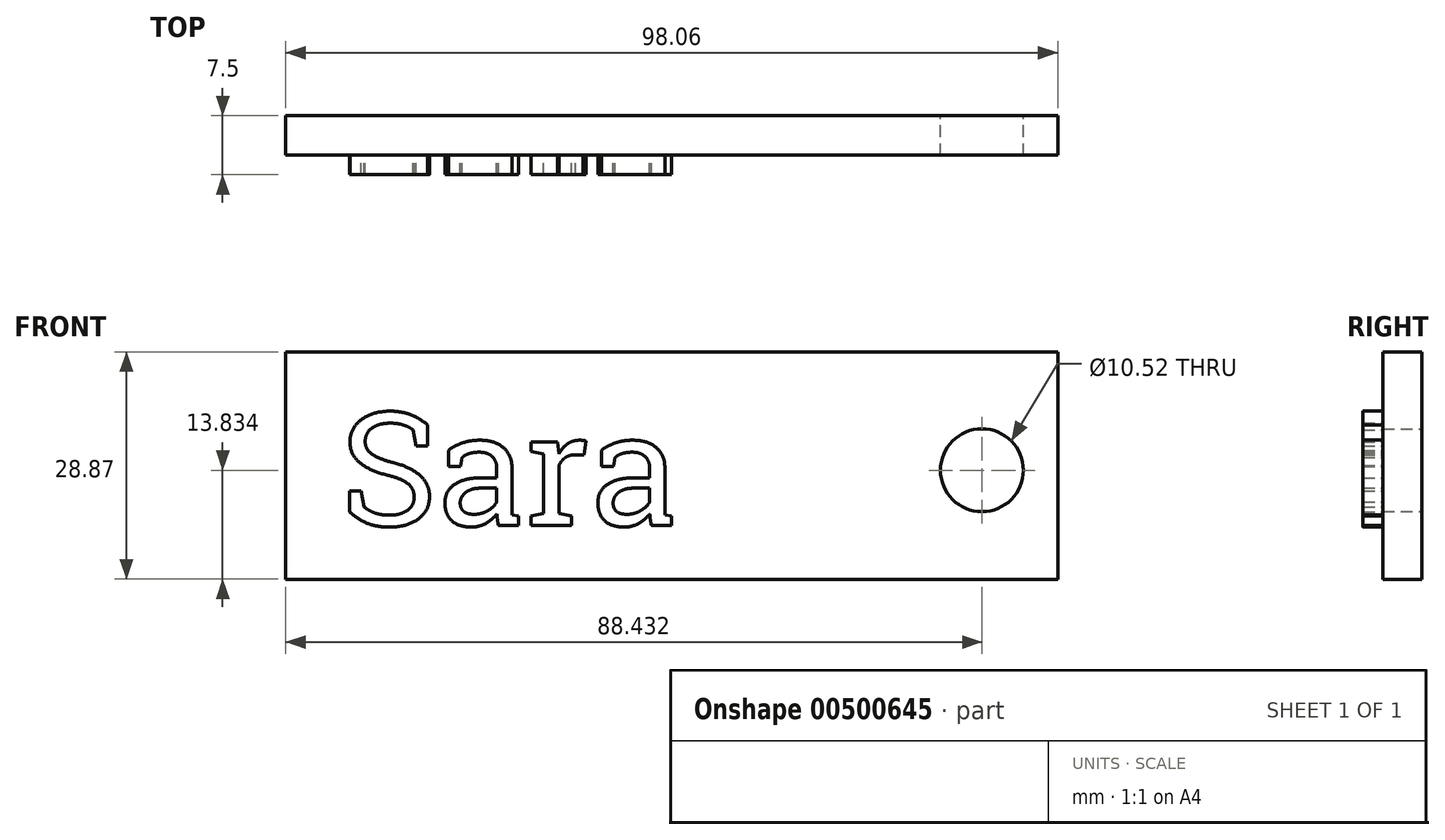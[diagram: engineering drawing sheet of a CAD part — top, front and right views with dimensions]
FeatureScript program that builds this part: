
annotation { "Feature Type Name" : "Feature", "Feature Type Description" : "" }
export const myFeature = defineFeature(function(context is Context, id is Id, definition is map)
    precondition{}
    {
        {
            var Q0;
            Q0=qCreatedBy(makeId("Front.planeOp"),FACE);
            var sketch = newSketch(context, id + "F0", { "sketchPlane" : qUnion([Q0])});
            skLineSegment(sketch, "E0.bottom", {"start": v(-64.67, 46.92) * mm, "end": v(33.39, 46.92) * mm});
            skLineSegment(sketch, "E0.top", {"start": v(-64.67, 18.05) * mm, "end": v(33.39, 18.05) * mm});
            skLineSegment(sketch, "E0.left", {"start": v(-64.67, 46.92) * mm, "end": v(-64.67, 18.05) * mm});
            skLineSegment(sketch, "E0.right", {"start": v(33.39, 46.92) * mm, "end": v(33.39, 18.05) * mm});
            skCircle(sketch, "E1", {"center": v(23.76, 31.88) * mm, "radius": 5.26 * mm});
            skSolve(sketch);
        }
        {
            var Q0;
            Q0 = qSketchRegion(id + "F0", true);
            extrude(context, id + "F1", {"entities" : qUnion([Q0]), "depth" : 5 * mm});
        }
        {
            var Q0;
            Q0 = qSketchRegion(id + "F0", true);
            extrude(context, id + "F2", {"entities" : qUnion([Q0]), "depth" : 5 * mm});
        }
        {
            var Q0;
            Q0=makeQuery(id+"F2.opExtrude","CAP_FACE",FACE,{"disambiguationData":[OSD([sQuery(id+"F0.wireOp",EDGE,"E0.bottom"),sQuery(id+"F0.wireOp",EDGE,"E0.top"),sQuery(id+"F0.wireOp",EDGE,"E0.left"),sQuery(id+"F0.wireOp",EDGE,"E0.right"),sQuery(id+"F0.wireOp",EDGE,"E1")])],"isStart":false});
            var sketch = newSketch(context, id + "F3", { "sketchPlane" : qUnion([Q0])});
            skText(sketch, "E2", { "text": "Sara", "fontName": "RobotoSlab-Regular.ttf"});
            const initialGuessF3  = {"E2": [-0.05773, 0.02487, 1, 0, 0.0145]};
            skSetInitialGuess(sketch, initialGuessF3);
            skSolve(sketch);
        }
        {
            var Q0;
            Q0 = qSketchRegion(id + "F3", true);
            var Q1;
            Q1 = qSketchRegion(id + "F0", true);
            extrude(context, id + "F4", {"entities" : qUnion([Q0, Q1]), "operationType" : NewBodyOperationType.ADD, "depth" : 2.5 * mm});
        }
    });
